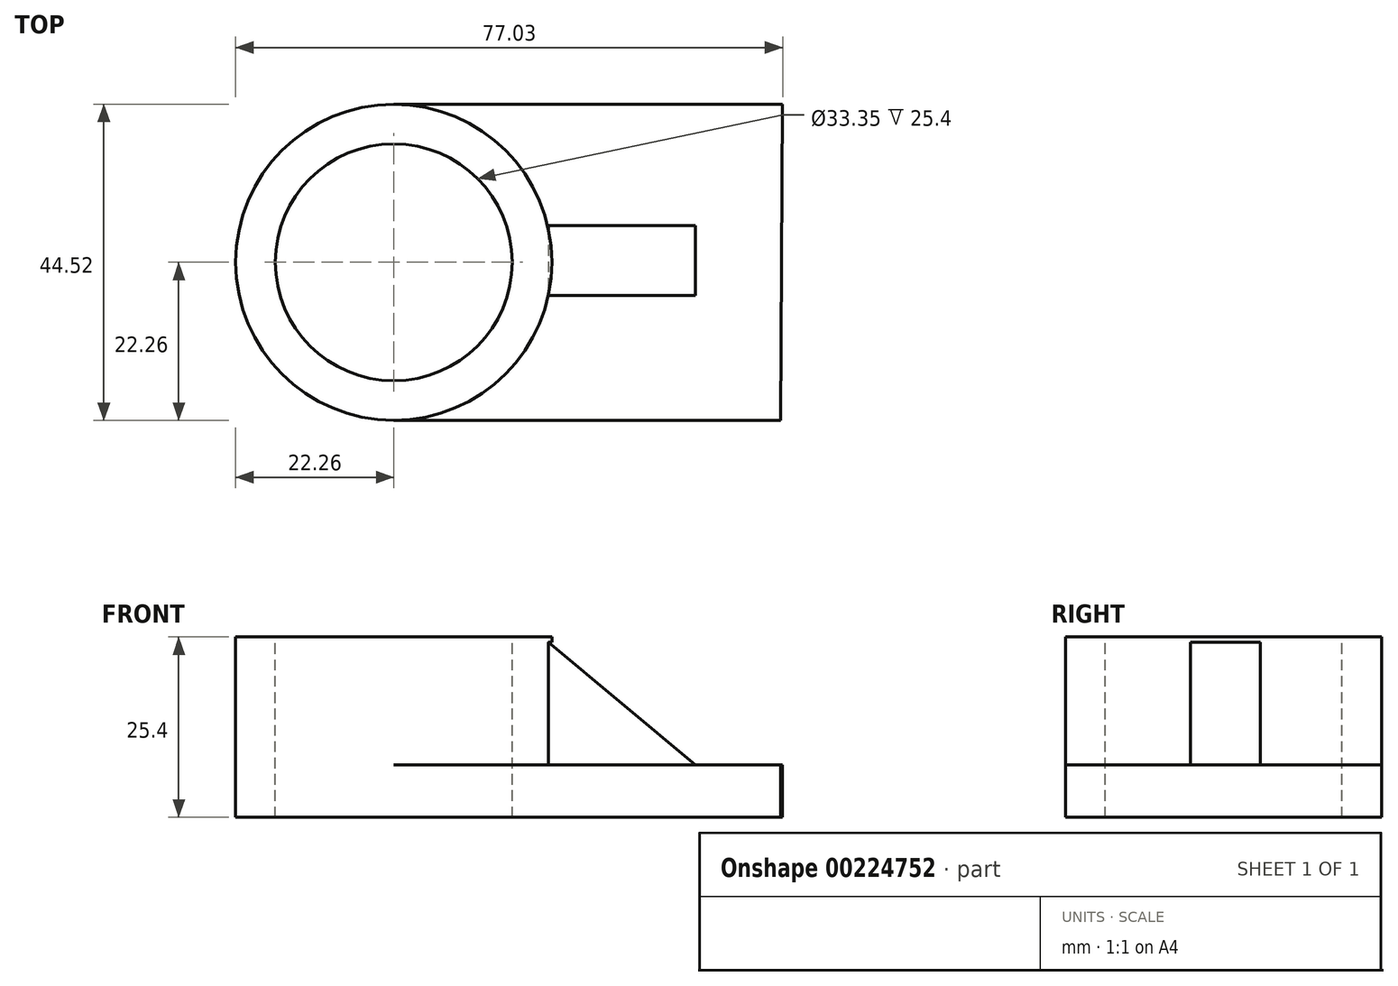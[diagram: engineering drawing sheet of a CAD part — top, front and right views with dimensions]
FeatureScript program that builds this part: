
annotation { "Feature Type Name" : "Feature", "Feature Type Description" : "" }
export const myFeature = defineFeature(function(context is Context, id is Id, definition is map)
    precondition{}
    {
        {
            var Q0;
            Q0=qCreatedBy(makeId("Top.planeOp"),FACE);
            var sketch = newSketch(context, id + "F0", { "sketchPlane" : qUnion([Q0])});
            skCircle(sketch, "E0", {"center": v(0, 0) * mm, "radius": 22.26 * mm});
            skSolve(sketch);
        }
        {
            var Q0;
            Q0=makeQuery(id+"F0.imprint","IMPRINT",FACE,{"disambiguationData":[TD([[makeQuery(id+"F0.imprint","IMPRINT",EDGE,{"derivedFrom":sQuery(id+"F0.wireOp",EDGE,"E0")}),1.0]])]});
            extrude(context, id + "F1", {"entities" : qUnion([Q0]), "depth" : 25.4 * mm});
        }
        {
            var Q0;
            Q0=makeQuery(id+"F1.opExtrude","CAP_FACE",FACE,{"disambiguationData":[OSD([sQuery(id+"F0.wireOp",EDGE,"E0")])],"isStart":true});
            var sketch = newSketch(context, id + "F2", { "sketchPlane" : qUnion([Q0])});
            skLineSegment(sketch, "E1", {"start": v(0, -22.26) * mm, "end": v(54.77, -22.26) * mm});
            skLineSegment(sketch, "E2", {"start": v(0, 22.26) * mm, "end": v(54.48, 22.26) * mm});
            skLineSegment(sketch, "E3", {"start": v(54.48, 22.26) * mm, "end": v(54.77, -22.26) * mm});
            skSolve(sketch);
        }
        {
            var Q0;
            {var subQ0=sQuery(id+"F2.wireOp",EDGE,"E1");Q0=makeQuery(id+"F2.imprint","IMPRINT",FACE,{"disambiguationData":[TD([[makeQuery(id+"F2.imprint","IMPRINT",EDGE,{"derivedFrom":subQ0}),1.0]])]});}
            extrude(context, id + "F3", {"entities" : qUnion([Q0]), "operationType" : NewBodyOperationType.ADD, "oppositeDirection" : true, "depth" : 7.37 * mm});
        }
        {
            var Q0;
            Q0=makeQuery(id+"F1.opExtrude","CAP_FACE",FACE,{"disambiguationData":[OSD([sQuery(id+"F0.wireOp",EDGE,"E0")])],"isStart":false});
            var sketch = newSketch(context, id + "F4", { "sketchPlane" : qUnion([Q0])});
            skCircle(sketch, "E4", {"center": v(0, 0) * mm, "radius": 16.67 * mm});
            skSolve(sketch);
        }
        {
            var Q0;
            Q0=makeQuery(id+"F4.imprint","IMPRINT",FACE,{"disambiguationData":[TD([[makeQuery(id+"F4.imprint","IMPRINT",EDGE,{"derivedFrom":sQuery(id+"F4.wireOp",EDGE,"E4")}),1.0]])]});
            extrude(context, id + "F5", {"entities" : qUnion([Q0]), "operationType" : NewBodyOperationType.REMOVE, "endBound" : BoundingType.THROUGH_ALL, "oppositeDirection" : true, "depth" : 25.4 * mm});
        }
        {
            var Q0;
            Q0=makeQuery(id+"F3.opExtrude","CAP_FACE",FACE,{"disambiguationData":[OSD([sQuery(id+"F0.wireOp",EDGE,"E0"),sQuery(id+"F2.wireOp",EDGE,"E1"),sQuery(id+"F2.wireOp",EDGE,"E2"),sQuery(id+"F2.wireOp",EDGE,"E3")])],"isStart":false});
            var sketch = newSketch(context, id + "F6", { "sketchPlane" : qUnion([Q0])});
            skLineSegment(sketch, "E5.bottom", {"start": v(21.66, 5.15) * mm, "end": v(42.5, 5.15) * mm});
            skLineSegment(sketch, "E5.top", {"start": v(21.66, -4.7) * mm, "end": v(42.5, -4.7) * mm});
            skLineSegment(sketch, "E5.left", {"start": v(21.66, 5.15) * mm, "end": v(21.66, -4.7) * mm});
            skLineSegment(sketch, "E5.right", {"start": v(42.5, 5.15) * mm, "end": v(42.5, -4.7) * mm});
            skSolve(sketch);
        }
        {
            var Q0;
            {var subQ0=sQuery(id+"F6.wireOp",EDGE,"E5.bottom");Q0=makeQuery(id+"F6.imprint","IMPRINT",FACE,{"disambiguationData":[TD([[makeQuery(id+"F6.imprint","IMPRINT",EDGE,{"derivedFrom":subQ0}),-1.0]])]});}
            extrude(context, id + "F7", {"entities" : qUnion([Q0]), "operationType" : NewBodyOperationType.ADD, "depth" : 17.27 * mm});
        }
        {
            var Q0;
            Q0=makeQuery(id+"F7.opExtrude","SWEPT_FACE",FACE,{"disambiguationData":[OSD([sQuery(id+"F6.wireOp",EDGE,"E5.top")])]});
            var sketch = newSketch(context, id + "F8", { "sketchPlane" : qUnion([Q0])});
            skLineSegment(sketch, "E6", {"start": v(21.76, 24.64) * mm, "end": v(42.5, 24.64) * mm});
            skLineSegment(sketch, "E7", {"start": v(42.5, 24.64) * mm, "end": v(42.5, 7.37) * mm});
            skLineSegment(sketch, "E8", {"start": v(42.5, 7.37) * mm, "end": v(21.76, 24.64) * mm});
            skSolve(sketch);
        }
        {
            var Q0;
            Q0=makeQuery(id+"F8.imprint","IMPRINT",FACE,{"disambiguationData":[TD([[makeQuery(id+"F8.imprint","IMPRINT",EDGE,{"derivedFrom":sQuery(id+"F8.wireOp",EDGE,"E6")}),-1.0]])]});
            extrude(context, id + "F9", {"entities" : qUnion([Q0]), "operationType" : NewBodyOperationType.REMOVE, "endBound" : BoundingType.THROUGH_ALL, "oppositeDirection" : true, "depth" : 25.4 * mm});
        }
    });
